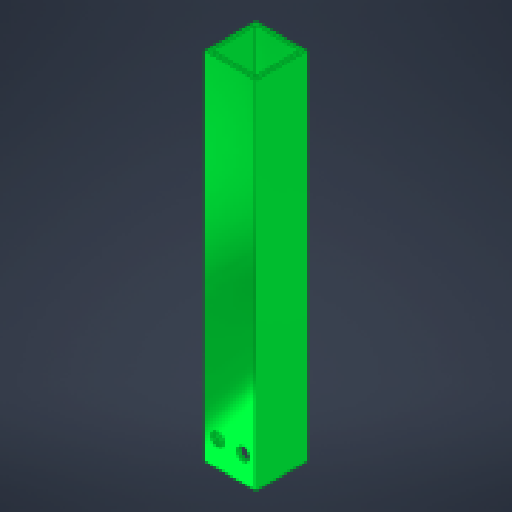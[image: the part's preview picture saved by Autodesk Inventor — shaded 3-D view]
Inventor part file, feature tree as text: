
AUTODESK INVENTOR PART (.ipt)
format: ipt  version: 2024 (Build 280153000, 153)  size: 158,720 bytes
history: native  units: mm
features: extrude x2, sketch x2, other x1
ambient origin geometry x8: Origin, YZ Plane, XZ Plane, XY Plane, X Axis, Y Axis, Z Axis, Center Point
bodies: Body1 (feature_tree)
feature tree (5):
  other  "Твердое тело1"
  extrude  "Выдавливание1"  Depth=20.0mm
  extrude  "Выдавливание2"  Depth=1.5mm
  sketch  "Эскиз1"
  sketch  "Эскиз2"
